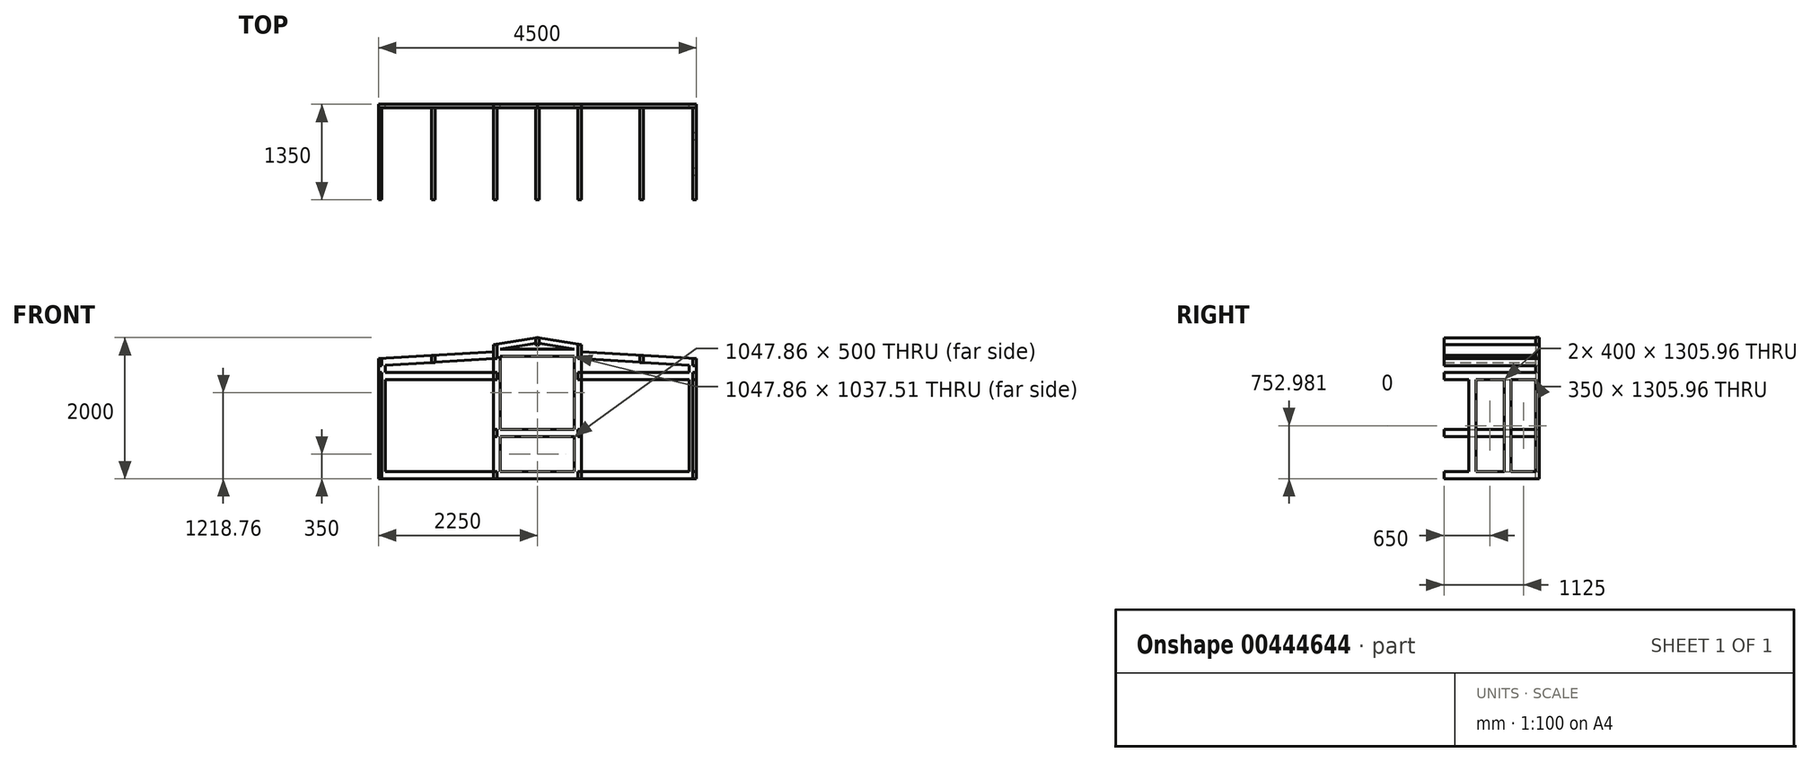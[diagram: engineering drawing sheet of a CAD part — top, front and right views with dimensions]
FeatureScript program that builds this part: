
annotation { "Feature Type Name" : "Feature", "Feature Type Description" : "" }
export const myFeature = defineFeature(function(context is Context, id is Id, definition is map)
    precondition{}
    {
        {
            var Q0;
            Q0=qCreatedBy(makeId("Front.planeOp"),FACE);
            var sketch = newSketch(context, id + "F0", { "sketchPlane" : qUnion([Q0])});
            skLineSegment(sketch, "E0", {"start": v(0, 0) * mm, "end": v(2250, 0) * mm});
            skLineSegment(sketch, "E1", {"start": v(2250, 0) * mm, "end": v(2250, 1700) * mm});
            skLineSegment(sketch, "E2", {"start": v(2250, 1700) * mm, "end": v(623.93, 1800) * mm});
            skLineSegment(sketch, "E3", {"start": v(623.93, 1800) * mm, "end": v(623.93, 1900) * mm});
            skLineSegment(sketch, "E4", {"start": v(623.93, 1900) * mm, "end": v(0, 2000) * mm});
            skLineSegment(sketch, "E5", {"start": v(0, 2000) * mm, "end": v(0, 0) * mm, "construction": true});
            skLineSegment(sketch, "E6", {"start": v(623.93, 1699.81) * mm, "end": v(623.93, 1505.96) * mm});
            skLineSegment(sketch, "E7", {"start": v(523.93, 600) * mm, "end": v(0, 600) * mm});
            skLineSegment(sketch, "E8", {"start": v(0, 1921.49) * mm, "end": v(523.93, 1837.51) * mm});
            skLineSegment(sketch, "E9", {"start": v(523.93, 1737.51) * mm, "end": v(523.93, 700) * mm});
            skLineSegment(sketch, "E10", {"start": v(523.93, 700) * mm, "end": v(0, 700) * mm});
            skLineSegment(sketch, "E11.0", {"start": v(2150, 1605.96) * mm, "end": v(617.8, 1700.19) * mm});
            skLineSegment(sketch, "E11.1", {"start": v(2150, 100) * mm, "end": v(2150, 1405.96) * mm});
            skLineSegment(sketch, "E11.2", {"start": v(0, 100) * mm, "end": v(523.93, 100) * mm});
            skLineSegment(sketch, "E12", {"start": v(623.93, 600) * mm, "end": v(623.93, 100) * mm});
            skLineSegment(sketch, "E13", {"start": v(523.93, 600) * mm, "end": v(523.93, 100) * mm});
            skLineSegment(sketch, "E14", {"start": v(623.93, 1505.96) * mm, "end": v(2150, 1505.96) * mm});
            skLineSegment(sketch, "E15", {"start": v(623.93, 1405.96) * mm, "end": v(2150, 1405.96) * mm});
            skLineSegment(sketch, "E16.trimOffspring", {"start": v(623.93, 1405.96) * mm, "end": v(623.93, 600) * mm});
            skLineSegment(sketch, "E17.trimOffspring", {"start": v(2150, 1505.96) * mm, "end": v(2150, 1605.96) * mm});
            skLineSegment(sketch, "E18.trimOffspring", {"start": v(623.93, 100) * mm, "end": v(2150, 100) * mm});
            skLineSegment(sketch, "E19.MirrorCS", {"start": v(-623.93, 1800) * mm, "end": v(-623.93, 1900) * mm});
            skLineSegment(sketch, "E20.MirrorCS", {"start": v(-2150, 1505.96) * mm, "end": v(-2150, 1605.96) * mm});
            skLineSegment(sketch, "E21.MirrorCS", {"start": v(-623.93, 1699.81) * mm, "end": v(-623.93, 1505.96) * mm});
            skLineSegment(sketch, "E22.MirrorCS", {"start": v(-623.93, 1505.96) * mm, "end": v(-2150, 1505.96) * mm});
            skLineSegment(sketch, "E23.MirrorCS", {"start": v(-623.93, 1405.96) * mm, "end": v(-623.93, 600) * mm});
            skLineSegment(sketch, "E24.MirrorCS", {"start": v(-523.93, 600) * mm, "end": v(-523.93, 100) * mm});
            skLineSegment(sketch, "E25.MirrorCS", {"start": v(-2150, 100) * mm, "end": v(-2150, 1405.96) * mm});
            skLineSegment(sketch, "E26.MirrorCS", {"start": v(0, 0) * mm, "end": v(-2250, 0) * mm});
            skLineSegment(sketch, "E27.MirrorCS", {"start": v(-623.93, 600) * mm, "end": v(-623.93, 100) * mm});
            skLineSegment(sketch, "E28.MirrorCS", {"start": v(-2250, 0) * mm, "end": v(-2250, 1700) * mm});
            skLineSegment(sketch, "E29.MirrorCS", {"start": v(-2250, 1700) * mm, "end": v(-623.93, 1800) * mm});
            skLineSegment(sketch, "E30.MirrorCS", {"start": v(-2150, 1605.96) * mm, "end": v(-617.8, 1700.19) * mm});
            skLineSegment(sketch, "E31.MirrorCS", {"start": v(0, 100) * mm, "end": v(-523.93, 100) * mm});
            skLineSegment(sketch, "E32.MirrorCS", {"start": v(-623.93, 1900) * mm, "end": v(0, 2000) * mm});
            skLineSegment(sketch, "E33.MirrorCS", {"start": v(-523.93, 600) * mm, "end": v(0, 600) * mm});
            skLineSegment(sketch, "E34.MirrorCS", {"start": v(-623.93, 1405.96) * mm, "end": v(-2150, 1405.96) * mm});
            skLineSegment(sketch, "E35.MirrorCS", {"start": v(0, 1921.49) * mm, "end": v(-523.93, 1837.51) * mm});
            skLineSegment(sketch, "E36.MirrorCS", {"start": v(-523.93, 1737.51) * mm, "end": v(-523.93, 700) * mm});
            skLineSegment(sketch, "E37.MirrorCS", {"start": v(-623.93, 100) * mm, "end": v(-2150, 100) * mm});
            skLineSegment(sketch, "E38.MirrorCS", {"start": v(-523.93, 700) * mm, "end": v(0, 700) * mm});
            skLineSegment(sketch, "E39", {"start": v(-523.93, 1837.51) * mm, "end": v(523.93, 1837.51) * mm});
            skLineSegment(sketch, "E40", {"start": v(-523.93, 1737.51) * mm, "end": v(523.93, 1737.51) * mm});
            skSolve(sketch);
        }
        {
            var Q0;
            Q0 = qSketchRegion(id + "F0", true);
            extrude(context, id + "F1", {"entities" : qUnion([Q0]), "depth" : 50 * mm});
        }
        {
            var Q0;
            Q0=makeQuery(id+"F1.opExtrude","CAP_FACE",FACE,{"disambiguationData":[OSD([sQuery(id+"F0.wireOp",EDGE,"E0"),sQuery(id+"F0.wireOp",EDGE,"E1"),sQuery(id+"F0.wireOp",EDGE,"E2"),sQuery(id+"F0.wireOp",EDGE,"E3"),sQuery(id+"F0.wireOp",EDGE,"E4"),sQuery(id+"F0.wireOp",EDGE,"E6"),sQuery(id+"F0.wireOp",EDGE,"E7"),sQuery(id+"F0.wireOp",EDGE,"E8"),sQuery(id+"F0.wireOp",EDGE,"E9"),sQuery(id+"F0.wireOp",EDGE,"E10"),sQuery(id+"F0.wireOp",EDGE,"E11.0"),sQuery(id+"F0.wireOp",EDGE,"E11.1"),sQuery(id+"F0.wireOp",EDGE,"E11.2"),sQuery(id+"F0.wireOp",EDGE,"E12"),sQuery(id+"F0.wireOp",EDGE,"E13"),sQuery(id+"F0.wireOp",EDGE,"E14"),sQuery(id+"F0.wireOp",EDGE,"E15"),sQuery(id+"F0.wireOp",EDGE,"E16.trimOffspring"),sQuery(id+"F0.wireOp",EDGE,"E17.trimOffspring"),sQuery(id+"F0.wireOp",EDGE,"E18.trimOffspring"),sQuery(id+"F0.wireOp",EDGE,"E19.MirrorCS"),sQuery(id+"F0.wireOp",EDGE,"E20.MirrorCS"),sQuery(id+"F0.wireOp",EDGE,"E21.MirrorCS"),sQuery(id+"F0.wireOp",EDGE,"E22.MirrorCS"),sQuery(id+"F0.wireOp",EDGE,"E23.MirrorCS"),sQuery(id+"F0.wireOp",EDGE,"E24.MirrorCS"),sQuery(id+"F0.wireOp",EDGE,"E25.MirrorCS"),sQuery(id+"F0.wireOp",EDGE,"E26.MirrorCS"),sQuery(id+"F0.wireOp",EDGE,"E27.MirrorCS"),sQuery(id+"F0.wireOp",EDGE,"E28.MirrorCS"),sQuery(id+"F0.wireOp",EDGE,"E29.MirrorCS"),sQuery(id+"F0.wireOp",EDGE,"E30.MirrorCS"),sQuery(id+"F0.wireOp",EDGE,"E31.MirrorCS"),sQuery(id+"F0.wireOp",EDGE,"E32.MirrorCS"),sQuery(id+"F0.wireOp",EDGE,"E33.MirrorCS"),sQuery(id+"F0.wireOp",EDGE,"E34.MirrorCS"),sQuery(id+"F0.wireOp",EDGE,"E35.MirrorCS"),sQuery(id+"F0.wireOp",EDGE,"E36.MirrorCS"),sQuery(id+"F0.wireOp",EDGE,"E37.MirrorCS"),sQuery(id+"F0.wireOp",EDGE,"E38.MirrorCS"),sQuery(id+"F0.wireOp",EDGE,"E39"),sQuery(id+"F0.wireOp",EDGE,"E40")])],"isStart":false});
            var sketch = newSketch(context, id + "F2", { "sketchPlane" : qUnion([Q0])});
            skLineSegment(sketch, "E41", {"start": v(-2250, 0) * mm, "end": v(-2250, 100) * mm});
            skLineSegment(sketch, "E42", {"start": v(-2250, 100) * mm, "end": v(-2200, 100) * mm});
            skLineSegment(sketch, "E43", {"start": v(-2200, 100) * mm, "end": v(-2200, 0) * mm});
            skLineSegment(sketch, "E44.bottom", {"start": v(-2250, 1700) * mm, "end": v(-2200, 1700) * mm});
            skLineSegment(sketch, "E44.top", {"start": v(-2250, 1600) * mm, "end": v(-2200, 1600) * mm});
            skLineSegment(sketch, "E44.left", {"start": v(-2250, 1700) * mm, "end": v(-2250, 1600) * mm});
            skLineSegment(sketch, "E44.right", {"start": v(-2200, 1700) * mm, "end": v(-2200, 1600) * mm});
            skLineSegment(sketch, "E45.bottom", {"start": v(-2250, 1505.96) * mm, "end": v(-2200, 1505.96) * mm});
            skLineSegment(sketch, "E45.top", {"start": v(-2250, 1405.96) * mm, "end": v(-2200, 1405.96) * mm});
            skLineSegment(sketch, "E45.left", {"start": v(-2250, 1505.96) * mm, "end": v(-2250, 1405.96) * mm});
            skLineSegment(sketch, "E45.right", {"start": v(-2200, 1505.96) * mm, "end": v(-2200, 1405.96) * mm});
            skLineSegment(sketch, "E46.bottom", {"start": v(-623.93, 1505.96) * mm, "end": v(-573.93, 1505.96) * mm});
            skLineSegment(sketch, "E46.top", {"start": v(-623.93, 1405.96) * mm, "end": v(-573.93, 1405.96) * mm});
            skLineSegment(sketch, "E46.left", {"start": v(-623.93, 1505.96) * mm, "end": v(-623.93, 1405.96) * mm});
            skLineSegment(sketch, "E46.right", {"start": v(-573.93, 1505.96) * mm, "end": v(-573.93, 1405.96) * mm});
            skPoint(sketch, "E47.oppositeSnap0", {"position": v(-573.93, 1455.96) * mm});
            skLineSegment(sketch, "E47.bottom", {"start": v(-623.93, 1900) * mm, "end": v(-573.93, 1900) * mm});
            skLineSegment(sketch, "E47.top", {"start": v(-623.93, 1699.81) * mm, "end": v(-573.93, 1699.81) * mm});
            skLineSegment(sketch, "E47.left", {"start": v(-623.93, 1900) * mm, "end": v(-623.93, 1699.81) * mm});
            skLineSegment(sketch, "E47.right", {"start": v(-573.93, 1900) * mm, "end": v(-573.93, 1699.81) * mm});
            skLineSegment(sketch, "E48.bottom", {"start": v(-1500, 1746.12) * mm, "end": v(-1450, 1746.12) * mm});
            skLineSegment(sketch, "E48.top", {"start": v(-1500, 1646.12) * mm, "end": v(-1450, 1646.12) * mm});
            skLineSegment(sketch, "E48.left", {"start": v(-1500, 1746.12) * mm, "end": v(-1500, 1646.12) * mm});
            skLineSegment(sketch, "E48.right", {"start": v(-1450, 1746.12) * mm, "end": v(-1450, 1646.12) * mm});
            skLineSegment(sketch, "E49.bottom", {"start": v(-623.93, 700) * mm, "end": v(-573.93, 700) * mm});
            skLineSegment(sketch, "E49.top", {"start": v(-623.93, 600) * mm, "end": v(-573.93, 600) * mm});
            skLineSegment(sketch, "E49.left", {"start": v(-623.93, 700) * mm, "end": v(-623.93, 600) * mm});
            skLineSegment(sketch, "E49.right", {"start": v(-573.93, 700) * mm, "end": v(-573.93, 600) * mm});
            skLineSegment(sketch, "E50.bottom", {"start": v(-573.93, 0) * mm, "end": v(-623.93, 0) * mm});
            skLineSegment(sketch, "E50.top", {"start": v(-573.93, 100) * mm, "end": v(-623.93, 100) * mm});
            skLineSegment(sketch, "E50.left", {"start": v(-573.93, 0) * mm, "end": v(-573.93, 100) * mm});
            skLineSegment(sketch, "E50.right", {"start": v(-623.93, 0) * mm, "end": v(-623.93, 100) * mm});
            skLineSegment(sketch, "E51.bottom", {"start": v(-25, 1996) * mm, "end": v(25, 1996) * mm});
            skLineSegment(sketch, "E51.top", {"start": v(-25, 1896) * mm, "end": v(25, 1896) * mm});
            skLineSegment(sketch, "E51.left", {"start": v(-25, 1996) * mm, "end": v(-25, 1896) * mm});
            skLineSegment(sketch, "E51.right", {"start": v(25, 1996) * mm, "end": v(25, 1896) * mm});
            skLineSegment(sketch, "E52", {"start": v(0, 600) * mm, "end": v(0, 700) * mm, "construction": true});
            skLineSegment(sketch, "E53.MirrorCS", {"start": v(2250, 1600) * mm, "end": v(2200, 1600) * mm});
            skLineSegment(sketch, "E54.MirrorCS", {"start": v(623.93, 1505.96) * mm, "end": v(573.93, 1505.96) * mm});
            skLineSegment(sketch, "E55.MirrorCS", {"start": v(623.93, 1699.81) * mm, "end": v(573.93, 1699.81) * mm});
            skLineSegment(sketch, "E56.MirrorCS", {"start": v(573.93, 0) * mm, "end": v(623.93, 0) * mm});
            skLineSegment(sketch, "E57.MirrorCS", {"start": v(1500, 1646.12) * mm, "end": v(1450, 1646.12) * mm});
            skLineSegment(sketch, "E58.MirrorCS", {"start": v(623.93, 700) * mm, "end": v(573.93, 700) * mm});
            skLineSegment(sketch, "E59.MirrorCS", {"start": v(573.93, 0) * mm, "end": v(573.93, 100) * mm});
            skLineSegment(sketch, "E60.MirrorCS", {"start": v(1500, 1746.12) * mm, "end": v(1450, 1746.12) * mm});
            skLineSegment(sketch, "E61.MirrorCS", {"start": v(573.93, 700) * mm, "end": v(573.93, 600) * mm});
            skLineSegment(sketch, "E62.MirrorCS", {"start": v(573.93, 100) * mm, "end": v(623.93, 100) * mm});
            skLineSegment(sketch, "E63.MirrorCS", {"start": v(623.93, 600) * mm, "end": v(573.93, 600) * mm});
            skLineSegment(sketch, "E64.MirrorCS", {"start": v(1500, 1746.12) * mm, "end": v(1500, 1646.12) * mm});
            skLineSegment(sketch, "E65.MirrorCS", {"start": v(623.93, 0) * mm, "end": v(623.93, 100) * mm});
            skLineSegment(sketch, "E66.MirrorCS", {"start": v(2200, 1700) * mm, "end": v(2200, 1600) * mm});
            skLineSegment(sketch, "E67.MirrorCS", {"start": v(2250, 1505.96) * mm, "end": v(2200, 1505.96) * mm});
            skLineSegment(sketch, "E68.MirrorCS", {"start": v(623.93, 1405.96) * mm, "end": v(573.93, 1405.96) * mm});
            skLineSegment(sketch, "E69.MirrorCS", {"start": v(2250, 1405.96) * mm, "end": v(2200, 1405.96) * mm});
            skLineSegment(sketch, "E70.MirrorCS", {"start": v(2250, 1505.96) * mm, "end": v(2250, 1405.96) * mm});
            skLineSegment(sketch, "E71.MirrorCS", {"start": v(2200, 1505.96) * mm, "end": v(2200, 1405.96) * mm});
            skLineSegment(sketch, "E72.MirrorCS", {"start": v(2250, 1700) * mm, "end": v(2250, 1600) * mm});
            skLineSegment(sketch, "E73.MirrorCS", {"start": v(623.93, 1505.96) * mm, "end": v(623.93, 1405.96) * mm});
            skLineSegment(sketch, "E74.MirrorCS", {"start": v(1450, 1746.12) * mm, "end": v(1450, 1646.12) * mm});
            skLineSegment(sketch, "E75.MirrorCS", {"start": v(573.93, 1505.96) * mm, "end": v(573.93, 1405.96) * mm});
            skLineSegment(sketch, "E76.MirrorCS", {"start": v(623.93, 700) * mm, "end": v(623.93, 600) * mm});
            skLineSegment(sketch, "E77.MirrorCS", {"start": v(2250, 1700) * mm, "end": v(2200, 1700) * mm});
            skLineSegment(sketch, "E78.MirrorCS", {"start": v(623.93, 1900) * mm, "end": v(573.93, 1900) * mm});
            skLineSegment(sketch, "E79.MirrorCS", {"start": v(2250, 100) * mm, "end": v(2200, 100) * mm});
            skLineSegment(sketch, "E80.MirrorCS", {"start": v(2200, 100) * mm, "end": v(2200, 0) * mm});
            skLineSegment(sketch, "E81.MirrorCS", {"start": v(2250, 0) * mm, "end": v(2250, 100) * mm});
            skLineSegment(sketch, "E82.MirrorCS", {"start": v(623.93, 1900) * mm, "end": v(623.93, 1699.81) * mm});
            skPoint(sketch, "E83.MirrorP", {"position": v(573.93, 1455.96) * mm});
            skLineSegment(sketch, "E84.MirrorCS", {"start": v(573.93, 1900) * mm, "end": v(573.93, 1699.81) * mm});
            skLineSegment(sketch, "E85.top", {"start": v(-2250, 0) * mm, "end": v(-2200, 0) * mm});
            skLineSegment(sketch, "E85.left", {"start": v(-2250, 100) * mm, "end": v(-2250, 0) * mm});
            skLineSegment(sketch, "E86.MirrorCS", {"start": v(2250, 100) * mm, "end": v(2250, 0) * mm});
            skLineSegment(sketch, "E87.MirrorCS", {"start": v(2250, 0) * mm, "end": v(2200, 0) * mm});
            skSolve(sketch);
        }
        {
            var Q0;
            Q0 = qSketchRegion(id + "F2", true);
            var Q1;
            {var subQ0=sQuery(id+"F2.wireOp",EDGE,"E41");Q1=makeQuery(id+"F2.imprint","IMPRINT",FACE,{"disambiguationData":[TD([[makeQuery(id+"F2.imprint","IMPRINT",EDGE,{"derivedFrom":subQ0}),-1.0]])]});}
            extrude(context, id + "F3", {"entities" : qUnion([Q0, Q1]), "operationType" : NewBodyOperationType.ADD, "depth" : 1300 * mm});
        }
        {
            var Q0;
            Q0=makeQuery(id+"F3.boolean.opBoolean","MERGE",FACE,{"derivedFrom":[makeQuery(id+"F1.opExtrude","SWEPT_FACE",FACE,{"disambiguationData":[OSD([sQuery(id+"F0.wireOp",EDGE,"E28.MirrorCS")])]}),makeQuery(id+"F3.opExtrude","SWEPT_FACE",FACE,{"disambiguationData":[OSD([sQuery(id+"F2.wireOp",EDGE,"E44.left")])]}),makeQuery(id+"F3.opExtrude","SWEPT_FACE",FACE,{"disambiguationData":[OSD([sQuery(id+"F2.wireOp",EDGE,"E45.left")])]}),makeQuery(id+"F3.opExtrude","SWEPT_FACE",FACE,{"disambiguationData":[OSD([sQuery(id+"F2.wireOp",EDGE,"E85.left")])]})]});
            var sketch = newSketch(context, id + "F4", { "sketchPlane" : qUnion([Q0])});
            skLineSegment(sketch, "E88", {"start": v(400, 1405.96) * mm, "end": v(400, 100) * mm});
            skLineSegment(sketch, "E89", {"start": v(400, 100) * mm, "end": v(500, 100) * mm});
            skLineSegment(sketch, "E90", {"start": v(500, 100) * mm, "end": v(500, 1405.96) * mm});
            skLineSegment(sketch, "E91", {"start": v(500, 1405.96) * mm, "end": v(400, 1405.96) * mm});
            skLineSegment(sketch, "E92", {"start": v(900, 1405.96) * mm, "end": v(900, 100) * mm});
            skLineSegment(sketch, "E93", {"start": v(900, 100) * mm, "end": v(1000, 100) * mm});
            skLineSegment(sketch, "E94", {"start": v(1000, 100) * mm, "end": v(1000, 1405.96) * mm});
            skLineSegment(sketch, "E95", {"start": v(1000, 1405.96) * mm, "end": v(900, 1405.96) * mm});
            skSolve(sketch);
        }
        {
            var Q0;
            Q0=makeQuery(id+"F4.imprint","IMPRINT",FACE,{"disambiguationData":[TD([[makeQuery(id+"F4.imprint","IMPRINT",EDGE,{"derivedFrom":sQuery(id+"F4.wireOp",EDGE,"E88")}),1.0]])]});
            var Q1;
            Q1=makeQuery(id+"F4.imprint","IMPRINT",FACE,{"disambiguationData":[TD([[makeQuery(id+"F4.imprint","IMPRINT",EDGE,{"derivedFrom":sQuery(id+"F4.wireOp",EDGE,"E92")}),1.0]])]});
            extrude(context, id + "F5", {"entities" : qUnion([Q0, Q1]), "operationType" : NewBodyOperationType.ADD, "oppositeDirection" : true, "depth" : 50 * mm});
        }
        {
            var Q0;
            Q0=makeQuery(id+"F3.boolean.opBoolean","MERGE",FACE,{"derivedFrom":[makeQuery(id+"F1.opExtrude","SWEPT_FACE",FACE,{"disambiguationData":[OSD([sQuery(id+"F0.wireOp",EDGE,"E1")])]}),makeQuery(id+"F3.opExtrude","SWEPT_FACE",FACE,{"disambiguationData":[OSD([sQuery(id+"F2.wireOp",EDGE,"E70.MirrorCS")])]}),makeQuery(id+"F3.opExtrude","SWEPT_FACE",FACE,{"disambiguationData":[OSD([sQuery(id+"F2.wireOp",EDGE,"E72.MirrorCS")])]}),makeQuery(id+"F3.opExtrude","SWEPT_FACE",FACE,{"disambiguationData":[OSD([sQuery(id+"F2.wireOp",EDGE,"E81.MirrorCS")])]})]});
            var sketch = newSketch(context, id + "F6", { "sketchPlane" : qUnion([Q0])});
            skLineSegment(sketch, "E96.bottom", {"start": v(-1000, 1405.96) * mm, "end": v(-900, 1405.96) * mm});
            skLineSegment(sketch, "E96.top", {"start": v(-1000, 100) * mm, "end": v(-900, 100) * mm});
            skLineSegment(sketch, "E96.left", {"start": v(-1000, 1405.96) * mm, "end": v(-1000, 100) * mm});
            skLineSegment(sketch, "E96.right", {"start": v(-900, 1405.96) * mm, "end": v(-900, 100) * mm});
            skLineSegment(sketch, "E97.bottom", {"start": v(-400, 1405.96) * mm, "end": v(-500, 1405.96) * mm});
            skLineSegment(sketch, "E97.top", {"start": v(-400, 100) * mm, "end": v(-500, 100) * mm});
            skLineSegment(sketch, "E97.left", {"start": v(-400, 1405.96) * mm, "end": v(-400, 100) * mm});
            skLineSegment(sketch, "E97.right", {"start": v(-500, 1405.96) * mm, "end": v(-500, 100) * mm});
            skSolve(sketch);
        }
        {
            var Q0;
            Q0 = qSketchRegion(id + "F6", true);
            extrude(context, id + "F7", {"entities" : qUnion([Q0]), "operationType" : NewBodyOperationType.ADD, "oppositeDirection" : true, "depth" : 50 * mm});
        }
    });
